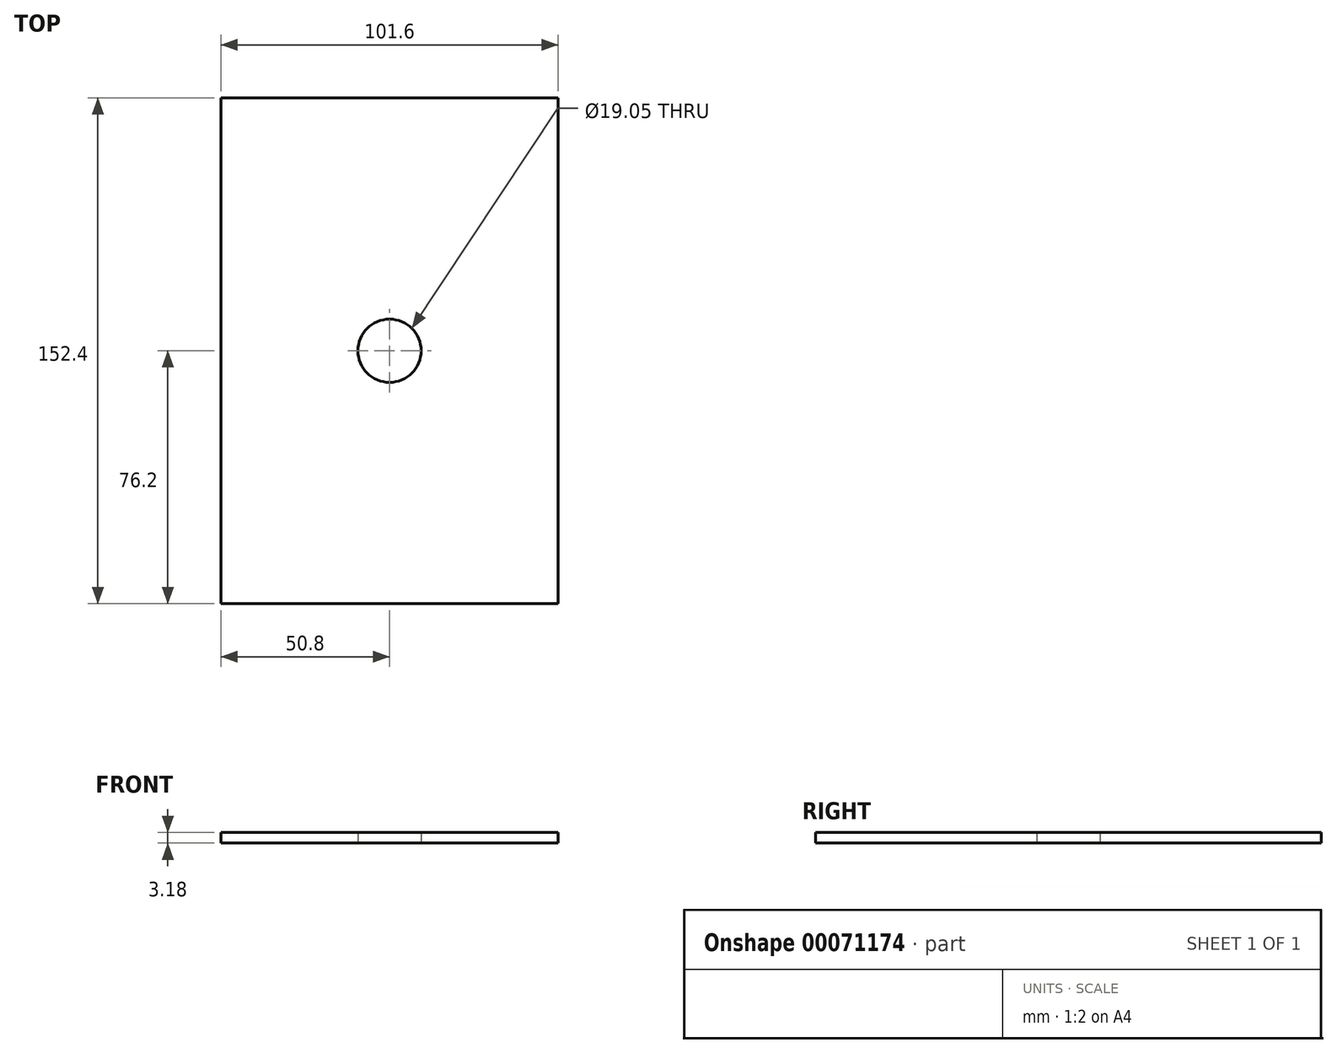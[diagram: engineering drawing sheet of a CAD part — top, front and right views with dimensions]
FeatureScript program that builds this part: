
annotation { "Feature Type Name" : "Feature", "Feature Type Description" : "" }
export const myFeature = defineFeature(function(context is Context, id is Id, definition is map)
    precondition{}
    {
        {
            var Q0;
            Q0=qCreatedBy(makeId("Top.planeOp"),FACE);
            var sketch = newSketch(context, id + "F0", { "sketchPlane" : qUnion([Q0])});
            skCircle(sketch, "E0", {"center": v(0, 0) * mm, "radius": 9.53 * mm});
            skLineSegment(sketch, "E1.rect.bottom", {"start": v(50.8, 76.2) * mm, "end": v(-50.8, 76.2) * mm});
            skLineSegment(sketch, "E1.rect.top", {"start": v(50.8, -76.2) * mm, "end": v(-50.8, -76.2) * mm});
            skLineSegment(sketch, "E1.rect.left", {"start": v(50.8, 76.2) * mm, "end": v(50.8, -76.2) * mm});
            skLineSegment(sketch, "E1.rect.right", {"start": v(-50.8, 76.2) * mm, "end": v(-50.8, -76.2) * mm});
            skSolve(sketch);
        }
        {
            var Q0;
            Q0 = qSketchRegion(id + "F0", true);
            extrude(context, id + "F1", {"entities" : qUnion([Q0]), "depth" : 3.17 * mm});
        }
    });
